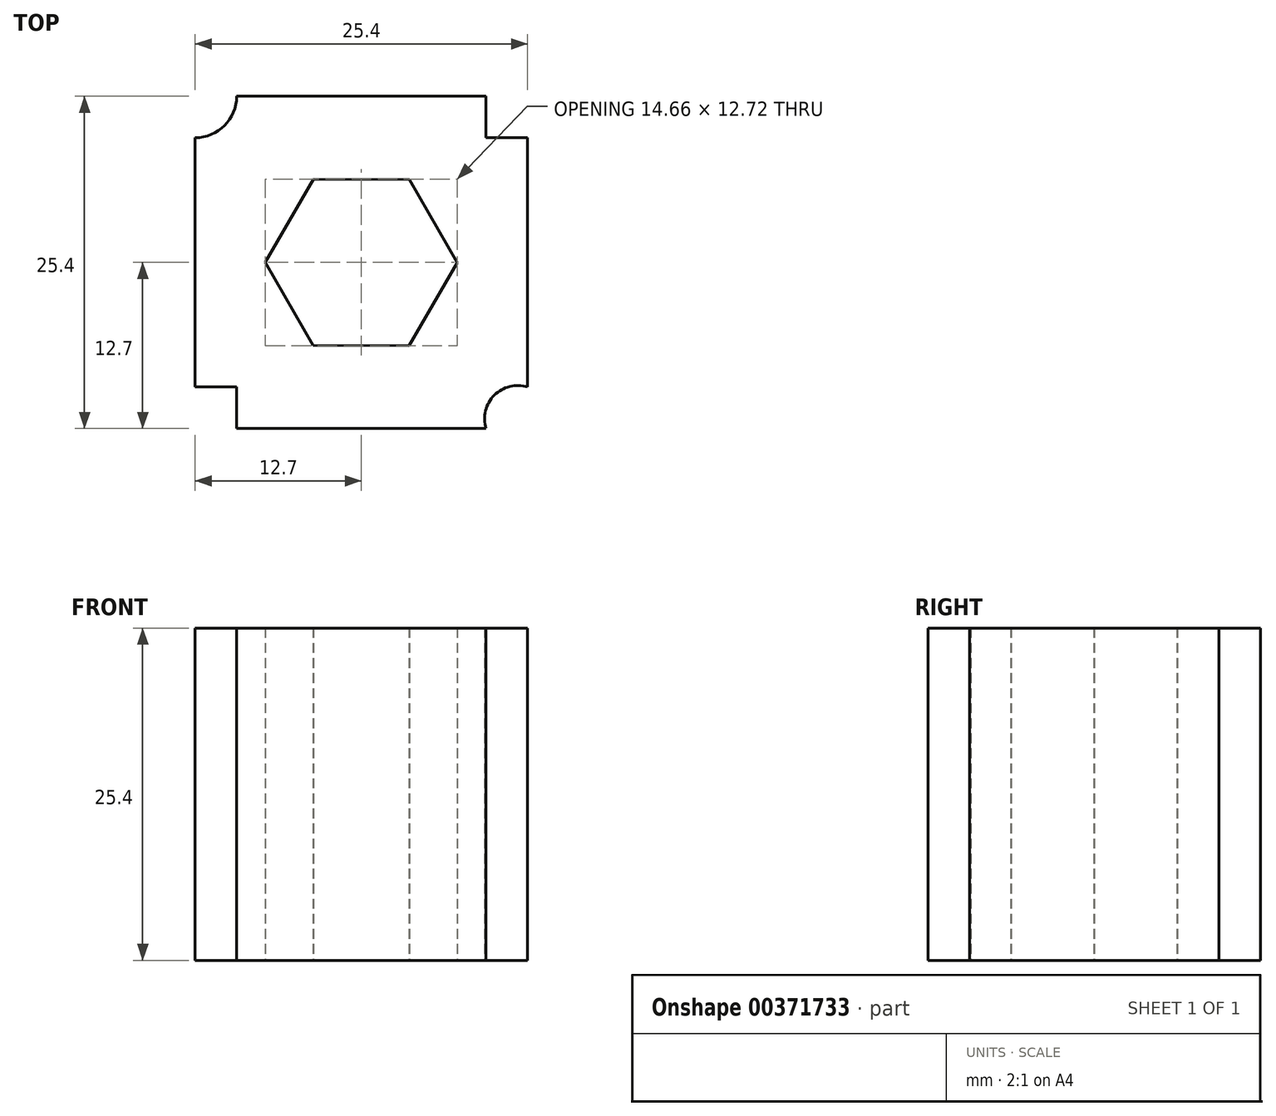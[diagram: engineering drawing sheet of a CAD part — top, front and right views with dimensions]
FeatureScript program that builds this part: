
annotation { "Feature Type Name" : "Feature", "Feature Type Description" : "" }
export const myFeature = defineFeature(function(context is Context, id is Id, definition is map)
    precondition{}
    {
        {
            var Q0;
            Q0=qCreatedBy(makeId("Top.planeOp"),FACE);
            var sketch = newSketch(context, id + "F0", { "sketchPlane" : qUnion([Q0])});
            skLineSegment(sketch, "E0.bottom", {"start": v(-12.7, 12.7) * mm, "end": v(12.7, 12.7) * mm});
            skLineSegment(sketch, "E0.top", {"start": v(-12.7, -12.7) * mm, "end": v(12.7, -12.7) * mm});
            skLineSegment(sketch, "E0.left", {"start": v(-12.7, 12.7) * mm, "end": v(-12.7, -12.7) * mm});
            skLineSegment(sketch, "E0.right", {"start": v(12.7, 12.7) * mm, "end": v(12.7, -12.7) * mm});
            skLineSegment(sketch, "E1", {"start": v(9.53, 12.7) * mm, "end": v(9.53, 9.52) * mm});
            skLineSegment(sketch, "E2", {"start": v(9.53, 9.52) * mm, "end": v(12.7, 9.52) * mm});
            skLineSegment(sketch, "E3", {"start": v(-12.7, -9.53) * mm, "end": v(-9.52, -9.53) * mm});
            skLineSegment(sketch, "E4", {"start": v(-9.52, -9.53) * mm, "end": v(-9.52, -12.7) * mm});
            skCircle(sketch, "E5.cCircle", {"center": v(0, 0) * mm, "radius": 6.35 * mm, "construction": true});
            skLineSegment(sketch, "E5.0", {"start": v(3.68, 6.34) * mm, "end": v(7.33, -0.02) * mm});
            skLineSegment(sketch, "E5.1", {"start": v(7.33, -0.02) * mm, "end": v(3.65, -6.36) * mm});
            skLineSegment(sketch, "E5.2", {"start": v(3.65, -6.36) * mm, "end": v(-3.68, -6.34) * mm});
            skLineSegment(sketch, "E5.3", {"start": v(-3.68, -6.34) * mm, "end": v(-7.33, 0.02) * mm});
            skLineSegment(sketch, "E5.4", {"start": v(-7.33, 0.02) * mm, "end": v(-3.65, 6.36) * mm});
            skLineSegment(sketch, "E5.5", {"start": v(-3.65, 6.36) * mm, "end": v(3.68, 6.34) * mm});
            skPoint(sketch, "E5.0.midPoint", {"position": v(5.5, 3.16) * mm});
            skArc(sketch, "E6", {"start": v(-12.7, 9.52) * mm, "mid": v(-10.45, 10.45) * mm, "end": v(-9.53, 12.7) * mm});
            skArc(sketch, "E7", {"start": v(12.7, -9.53) * mm, "mid": v(10.16, -10.16) * mm, "end": v(9.52, -12.7) * mm});
            skSolve(sketch);
        }
        {
            var Q0;
            {var subQ2=sQuery(id+"F0.wireOp",EDGE,"E1");Q0=makeQuery(id+"F0.imprint","IMPRINT",FACE,{"disambiguationData":[TD([[makeQuery(id+"F0.imprint","IMPRINT",EDGE,{"derivedFrom":subQ2}),-1.0]])]});}
            extrude(context, id + "F1", {"entities" : qUnion([Q0]), "depth" : 25.4 * mm});
        }
    });
